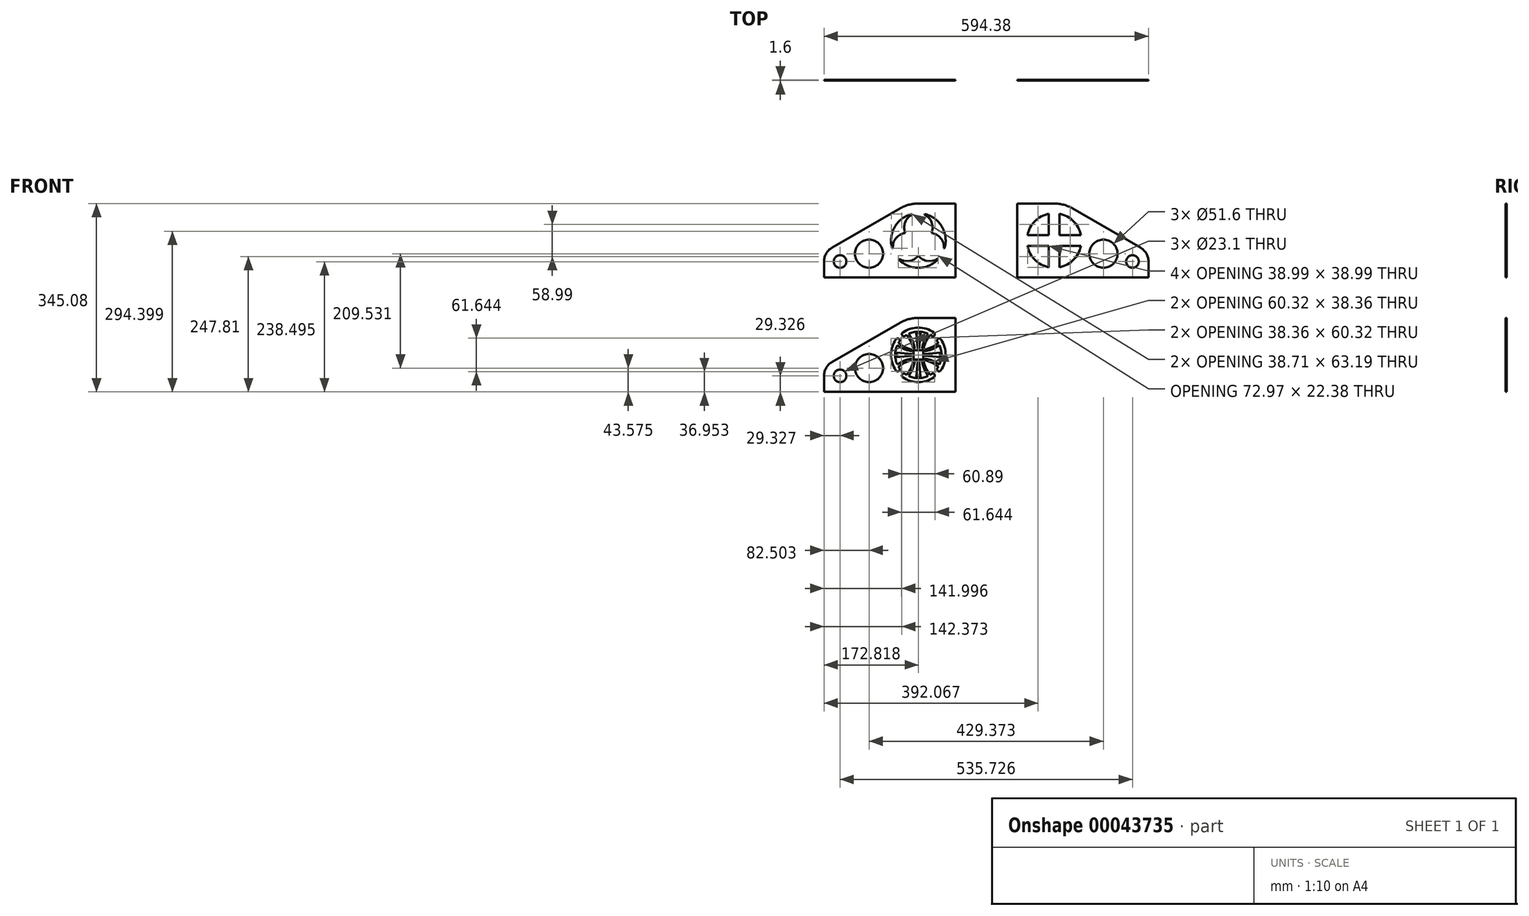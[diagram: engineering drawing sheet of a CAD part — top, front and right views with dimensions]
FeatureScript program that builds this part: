
annotation { "Feature Type Name" : "Feature", "Feature Type Description" : "" }
export const myFeature = defineFeature(function(context is Context, id is Id, definition is map)
    precondition{}
    {
        {
            var Q0;
            Q0=qCreatedBy(makeId("Front.planeOp"),FACE);
            var sketch = newSketch(context, id + "F0", { "sketchPlane" : qUnion([Q0])});
            skLineSegment(sketch, "E0", {"start": v(-56.6, -172.54) * mm, "end": v(-297.19, -172.54) * mm});
            skLineSegment(sketch, "E1", {"start": v(-124.37, -37) * mm, "end": v(-56.6, -37) * mm});
            skArc(sketch, "E2", {"start": v(-124.37, -37) * mm, "mid": v(-141.91, -39.3) * mm, "end": v(-158.26, -46.07) * mm});
            skLineSegment(sketch, "E3", {"start": v(-282.52, -117.82) * mm, "end": v(-158.26, -46.07) * mm});
            skArc(sketch, "E4", {"start": v(-282.52, -117.82) * mm, "mid": v(-293.26, -128.55) * mm, "end": v(-297.19, -143.21) * mm});
            skLineSegment(sketch, "E5", {"start": v(-297.19, -143.21) * mm, "end": v(-297.19, -172.54) * mm});
            skCircle(sketch, "E6", {"center": v(-214.69, -128.97) * mm, "radius": 25.8 * mm});
            skCircle(sketch, "E7", {"center": v(-267.86, -143.21) * mm, "radius": 11.55 * mm});
            skLineSegment(sketch, "E8", {"start": v(-56.6, -37) * mm, "end": v(-56.6, -172.54) * mm});
            skLineSegment(sketch, "E9", {"start": v(-56.6, 37) * mm, "end": v(-297.19, 37) * mm});
            skArc(sketch, "E10", {"start": v(-135.74, 153.46) * mm, "mid": v(-167.67, 129.77) * mm, "end": v(-172.22, 90.26) * mm});
            skArc(sketch, "E11", {"start": v(-100.45, 118.58) * mm, "mid": v(-100.07, 138.01) * mm, "end": v(-113.28, 152.28) * mm});
            skArc(sketch, "E12", {"start": v(-124.37, 77.14) * mm, "mid": v(-107.73, 67.1) * mm, "end": v(-88.77, 71.4) * mm});
            skArc(sketch, "E13", {"start": v(-148.3, 118.58) * mm, "mid": v(-165.32, 109.18) * mm, "end": v(-171.07, 90.61) * mm});
            skLineSegment(sketch, "E14", {"start": v(-135.46, 152.28) * mm, "end": v(-135.74, 153.46) * mm});
            skLineSegment(sketch, "E15", {"start": v(-113.28, 152.28) * mm, "end": v(-113, 153.46) * mm});
            skArc(sketch, "E16", {"start": v(-135.46, 152.28) * mm, "mid": v(-148.67, 138.01) * mm, "end": v(-148.3, 118.58) * mm});
            skLineSegment(sketch, "E17", {"start": v(-159.98, 71.4) * mm, "end": v(-160.86, 70.58) * mm});
            skLineSegment(sketch, "E18", {"start": v(-171.07, 90.61) * mm, "end": v(-172.22, 90.26) * mm});
            skLineSegment(sketch, "E19", {"start": v(-77.68, 90.61) * mm, "end": v(-76.52, 90.26) * mm});
            skLineSegment(sketch, "E20", {"start": v(-88.77, 71.4) * mm, "end": v(-87.89, 70.58) * mm});
            skArc(sketch, "E21", {"start": v(-76.52, 90.26) * mm, "mid": v(-81.07, 129.77) * mm, "end": v(-113, 153.46) * mm});
            skArc(sketch, "E22", {"start": v(-77.68, 90.61) * mm, "mid": v(-83.43, 109.18) * mm, "end": v(-100.45, 118.58) * mm});
            skArc(sketch, "E23", {"start": v(-159.98, 71.4) * mm, "mid": v(-141.02, 67.1) * mm, "end": v(-124.37, 77.14) * mm});
            skArc(sketch, "E24", {"start": v(-160.86, 70.58) * mm, "mid": v(-124.37, 54.77) * mm, "end": v(-87.89, 70.58) * mm});
            skLineSegment(sketch, "E25", {"start": v(-124.37, 172.54) * mm, "end": v(-56.6, 172.54) * mm});
            skArc(sketch, "E26", {"start": v(-124.37, 172.54) * mm, "mid": v(-141.91, 170.23) * mm, "end": v(-158.26, 163.46) * mm});
            skLineSegment(sketch, "E27", {"start": v(-282.52, 91.71) * mm, "end": v(-158.26, 163.46) * mm});
            skArc(sketch, "E28", {"start": v(-282.52, 91.71) * mm, "mid": v(-293.26, 80.98) * mm, "end": v(-297.19, 66.32) * mm});
            skLineSegment(sketch, "E29", {"start": v(-297.19, 66.32) * mm, "end": v(-297.19, 37) * mm});
            skCircle(sketch, "E30", {"center": v(-214.69, 80.57) * mm, "radius": 25.8 * mm});
            skCircle(sketch, "E31", {"center": v(-267.86, 66.32) * mm, "radius": 11.55 * mm});
            skLineSegment(sketch, "E32", {"start": v(-56.6, 172.54) * mm, "end": v(-56.6, 37) * mm});
            skLineSegment(sketch, "E33", {"start": v(282.52, 91.71) * mm, "end": v(158.26, 163.46) * mm});
            skLineSegment(sketch, "E34", {"start": v(297.19, 37) * mm, "end": v(56.6, 37) * mm});
            skArc(sketch, "E35", {"start": v(134.37, 55.78) * mm, "mid": v(159.73, 69.41) * mm, "end": v(173.36, 94.77) * mm});
            skLineSegment(sketch, "E36", {"start": v(75.38, 114.77) * mm, "end": v(114.37, 114.77) * mm});
            skLineSegment(sketch, "E37", {"start": v(75.38, 94.77) * mm, "end": v(114.37, 94.77) * mm});
            skLineSegment(sketch, "E38", {"start": v(134.37, 153.76) * mm, "end": v(134.37, 114.77) * mm});
            skLineSegment(sketch, "E39", {"start": v(114.37, 153.76) * mm, "end": v(114.37, 114.77) * mm});
            skLineSegment(sketch, "E40", {"start": v(134.37, 94.77) * mm, "end": v(173.36, 94.77) * mm});
            skLineSegment(sketch, "E41", {"start": v(114.37, 94.77) * mm, "end": v(114.37, 55.78) * mm});
            skLineSegment(sketch, "E42", {"start": v(134.37, 114.77) * mm, "end": v(173.36, 114.77) * mm});
            skLineSegment(sketch, "E43", {"start": v(134.37, 94.77) * mm, "end": v(134.37, 55.78) * mm});
            skArc(sketch, "E44", {"start": v(75.38, 94.77) * mm, "mid": v(89.02, 69.41) * mm, "end": v(114.37, 55.78) * mm});
            skArc(sketch, "E45", {"start": v(114.37, 153.76) * mm, "mid": v(89.02, 140.12) * mm, "end": v(75.38, 114.77) * mm});
            skArc(sketch, "E46", {"start": v(173.36, 114.77) * mm, "mid": v(159.73, 140.12) * mm, "end": v(134.37, 153.76) * mm});
            skCircle(sketch, "E47", {"center": v(214.69, 80.57) * mm, "radius": 25.8 * mm});
            skCircle(sketch, "E48", {"center": v(267.86, 66.32) * mm, "radius": 11.55 * mm});
            skArc(sketch, "E49", {"start": v(158.26, 163.46) * mm, "mid": v(141.91, 170.23) * mm, "end": v(124.37, 172.54) * mm});
            skLineSegment(sketch, "E50", {"start": v(124.37, 172.54) * mm, "end": v(56.6, 172.54) * mm});
            skArc(sketch, "E51", {"start": v(297.19, 66.32) * mm, "mid": v(293.26, 80.98) * mm, "end": v(282.52, 91.71) * mm});
            skLineSegment(sketch, "E52", {"start": v(297.19, 66.32) * mm, "end": v(297.19, 37) * mm});
            skLineSegment(sketch, "E53", {"start": v(56.6, 172.54) * mm, "end": v(56.6, 37) * mm});
            skArc(sketch, "E54", {"start": v(-134.02, -93.12) * mm, "mid": v(-138.57, -79.96) * mm, "end": v(-146.3, -68.38) * mm});
            skArc(sketch, "E55", {"start": v(-131.07, -93.12) * mm, "mid": v(-135.05, -79.02) * mm, "end": v(-142, -66.12) * mm});
            skLineSegment(sketch, "E56", {"start": v(-128.36, -64.84) * mm, "end": v(-125.85, -93.12) * mm});
            skArc(sketch, "E57", {"start": v(-102.45, -68.38) * mm, "mid": v(-110.18, -79.96) * mm, "end": v(-114.73, -93.12) * mm});
            skArc(sketch, "E58", {"start": v(-106.74, -66.12) * mm, "mid": v(-113.7, -79.02) * mm, "end": v(-117.67, -93.12) * mm});
            skLineSegment(sketch, "E59", {"start": v(-120.39, -64.84) * mm, "end": v(-122.9, -93.12) * mm});
            skLineSegment(sketch, "E60", {"start": v(-128.36, -64.84) * mm, "end": v(-120.39, -64.84) * mm});
            skLineSegment(sketch, "E61", {"start": v(-133.07, -96.07) * mm, "end": v(-133.07, -113.46) * mm});
            skLineSegment(sketch, "E62", {"start": v(-133.07, -113.46) * mm, "end": v(-115.68, -113.46) * mm});
            skLineSegment(sketch, "E63", {"start": v(-115.68, -113.46) * mm, "end": v(-115.68, -96.07) * mm});
            skLineSegment(sketch, "E64", {"start": v(-115.68, -96.07) * mm, "end": v(-133.07, -96.07) * mm});
            skArc(sketch, "E65", {"start": v(-100.06, -69.93) * mm, "mid": v(-94.83, -69) * mm, "end": v(-95.76, -63.76) * mm});
            skArc(sketch, "E66", {"start": v(-152.98, -63.76) * mm, "mid": v(-153.92, -69) * mm, "end": v(-148.68, -69.93) * mm});
            skArc(sketch, "E67", {"start": v(-95.76, -63.76) * mm, "mid": v(-124.37, -54.77) * mm, "end": v(-152.98, -63.76) * mm});
            skArc(sketch, "E68", {"start": v(-100.06, -69.93) * mm, "mid": v(-101.25, -69.13) * mm, "end": v(-102.45, -68.38) * mm});
            skArc(sketch, "E69", {"start": v(-146.3, -68.38) * mm, "mid": v(-147.5, -69.13) * mm, "end": v(-148.68, -69.93) * mm});
            skArc(sketch, "E70", {"start": v(-136.02, -114.4) * mm, "mid": v(-149.17, -118.96) * mm, "end": v(-160.76, -126.68) * mm});
            skArc(sketch, "E71", {"start": v(-106.74, -66.12) * mm, "mid": v(-124.37, -62.29) * mm, "end": v(-142, -66.12) * mm});
            skArc(sketch, "E72", {"start": v(-136.02, -111.46) * mm, "mid": v(-150.12, -115.44) * mm, "end": v(-163.02, -122.4) * mm});
            skLineSegment(sketch, "E73", {"start": v(-164.3, -108.75) * mm, "end": v(-136.02, -106.24) * mm});
            skArc(sketch, "E74", {"start": v(-160.76, -82.85) * mm, "mid": v(-149.17, -90.57) * mm, "end": v(-136.02, -95.12) * mm});
            skArc(sketch, "E75", {"start": v(-163.02, -87.13) * mm, "mid": v(-150.12, -94.09) * mm, "end": v(-136.02, -98.07) * mm});
            skLineSegment(sketch, "E76", {"start": v(-164.3, -100.78) * mm, "end": v(-136.02, -103.3) * mm});
            skLineSegment(sketch, "E77", {"start": v(-164.3, -108.75) * mm, "end": v(-164.3, -100.78) * mm});
            skArc(sketch, "E78", {"start": v(-165.38, -133.38) * mm, "mid": v(-160.14, -134.3) * mm, "end": v(-159.2, -129.07) * mm});
            skArc(sketch, "E79", {"start": v(-159.2, -80.46) * mm, "mid": v(-160.14, -75.22) * mm, "end": v(-165.38, -76.15) * mm});
            skArc(sketch, "E80", {"start": v(-165.38, -76.15) * mm, "mid": v(-174.37, -104.77) * mm, "end": v(-165.38, -133.38) * mm});
            skArc(sketch, "E81", {"start": v(-159.2, -80.46) * mm, "mid": v(-160, -81.64) * mm, "end": v(-160.76, -82.85) * mm});
            skArc(sketch, "E82", {"start": v(-160.76, -126.68) * mm, "mid": v(-160, -127.9) * mm, "end": v(-159.2, -129.07) * mm});
            skArc(sketch, "E83", {"start": v(-163.02, -87.13) * mm, "mid": v(-166.85, -104.77) * mm, "end": v(-163.02, -122.4) * mm});
            skArc(sketch, "E84", {"start": v(-114.73, -116.4) * mm, "mid": v(-110.18, -129.57) * mm, "end": v(-102.45, -141.15) * mm});
            skArc(sketch, "E85", {"start": v(-117.67, -116.4) * mm, "mid": v(-113.7, -130.51) * mm, "end": v(-106.74, -143.41) * mm});
            skLineSegment(sketch, "E86", {"start": v(-120.39, -144.7) * mm, "end": v(-122.9, -116.4) * mm});
            skArc(sketch, "E87", {"start": v(-146.3, -141.15) * mm, "mid": v(-138.57, -129.57) * mm, "end": v(-134.02, -116.4) * mm});
            skArc(sketch, "E88", {"start": v(-142, -143.41) * mm, "mid": v(-135.05, -130.51) * mm, "end": v(-131.07, -116.4) * mm});
            skLineSegment(sketch, "E89", {"start": v(-128.36, -144.7) * mm, "end": v(-125.85, -116.4) * mm});
            skLineSegment(sketch, "E90", {"start": v(-120.39, -144.7) * mm, "end": v(-128.36, -144.7) * mm});
            skArc(sketch, "E91", {"start": v(-95.76, -145.77) * mm, "mid": v(-94.83, -140.53) * mm, "end": v(-100.06, -139.6) * mm});
            skArc(sketch, "E92", {"start": v(-148.68, -139.6) * mm, "mid": v(-153.92, -140.53) * mm, "end": v(-152.98, -145.77) * mm});
            skArc(sketch, "E93", {"start": v(-152.98, -145.77) * mm, "mid": v(-124.37, -154.77) * mm, "end": v(-95.76, -145.77) * mm});
            skArc(sketch, "E94", {"start": v(-148.68, -139.6) * mm, "mid": v(-147.5, -140.4) * mm, "end": v(-146.3, -141.15) * mm});
            skArc(sketch, "E95", {"start": v(-102.45, -141.15) * mm, "mid": v(-101.25, -140.4) * mm, "end": v(-100.06, -139.6) * mm});
            skArc(sketch, "E96", {"start": v(-142, -143.41) * mm, "mid": v(-124.37, -147.24) * mm, "end": v(-106.74, -143.41) * mm});
            skArc(sketch, "E97", {"start": v(-112.73, -95.12) * mm, "mid": v(-99.57, -90.57) * mm, "end": v(-87.99, -82.85) * mm});
            skArc(sketch, "E98", {"start": v(-112.73, -98.07) * mm, "mid": v(-98.62, -94.09) * mm, "end": v(-85.73, -87.13) * mm});
            skLineSegment(sketch, "E99", {"start": v(-84.44, -100.78) * mm, "end": v(-112.73, -103.3) * mm});
            skArc(sketch, "E100", {"start": v(-87.99, -126.68) * mm, "mid": v(-99.57, -118.96) * mm, "end": v(-112.73, -114.4) * mm});
            skArc(sketch, "E101", {"start": v(-85.73, -122.4) * mm, "mid": v(-98.62, -115.44) * mm, "end": v(-112.73, -111.46) * mm});
            skLineSegment(sketch, "E102", {"start": v(-84.44, -108.75) * mm, "end": v(-112.73, -106.24) * mm});
            skLineSegment(sketch, "E103", {"start": v(-84.44, -100.78) * mm, "end": v(-84.44, -108.75) * mm});
            skArc(sketch, "E104", {"start": v(-83.37, -76.15) * mm, "mid": v(-88.6, -75.22) * mm, "end": v(-89.54, -80.46) * mm});
            skArc(sketch, "E105", {"start": v(-89.54, -129.07) * mm, "mid": v(-88.6, -134.3) * mm, "end": v(-83.37, -133.38) * mm});
            skArc(sketch, "E106", {"start": v(-83.37, -133.38) * mm, "mid": v(-74.37, -104.77) * mm, "end": v(-83.37, -76.15) * mm});
            skArc(sketch, "E107", {"start": v(-89.54, -129.07) * mm, "mid": v(-88.74, -127.9) * mm, "end": v(-87.99, -126.68) * mm});
            skArc(sketch, "E108", {"start": v(-87.99, -82.85) * mm, "mid": v(-88.74, -81.64) * mm, "end": v(-89.54, -80.46) * mm});
            skArc(sketch, "E109", {"start": v(-85.73, -122.4) * mm, "mid": v(-81.9, -104.77) * mm, "end": v(-85.73, -87.13) * mm});
            skLineSegment(sketch, "E110", {"start": v(-114.73, -116.4) * mm, "end": v(-117.67, -116.4) * mm});
            skLineSegment(sketch, "E111", {"start": v(-112.73, -111.46) * mm, "end": v(-112.73, -114.4) * mm});
            skLineSegment(sketch, "E112", {"start": v(-131.07, -116.4) * mm, "end": v(-134.02, -116.4) * mm});
            skLineSegment(sketch, "E113", {"start": v(-122.9, -116.4) * mm, "end": v(-125.85, -116.4) * mm});
            skLineSegment(sketch, "E114", {"start": v(-112.73, -103.3) * mm, "end": v(-112.73, -106.24) * mm});
            skLineSegment(sketch, "E115", {"start": v(-136.02, -106.24) * mm, "end": v(-136.02, -103.3) * mm});
            skLineSegment(sketch, "E116", {"start": v(-136.02, -114.4) * mm, "end": v(-136.02, -111.46) * mm});
            skLineSegment(sketch, "E117", {"start": v(-112.73, -95.12) * mm, "end": v(-112.73, -98.07) * mm});
            skLineSegment(sketch, "E118", {"start": v(-117.67, -93.12) * mm, "end": v(-114.73, -93.12) * mm});
            skLineSegment(sketch, "E119", {"start": v(-136.02, -95.12) * mm, "end": v(-136.02, -98.07) * mm});
            skLineSegment(sketch, "E120", {"start": v(-125.85, -93.12) * mm, "end": v(-122.9, -93.12) * mm});
            skLineSegment(sketch, "E121", {"start": v(-134.02, -93.12) * mm, "end": v(-131.07, -93.12) * mm});
            skSolve(sketch);
        }
        {
            var Q0;
            Q0=makeQuery(id+"F0.imprint","IMPRINT",FACE,{"disambiguationData":[TD([[makeQuery(id+"F0.imprint","IMPRINT",EDGE,{"derivedFrom":sQuery(id+"F0.wireOp",EDGE,"E9")}),-1.0]])]});
            extrude(context, id + "F1", {"entities" : qUnion([Q0]), "depth" : 1.6 * mm});
        }
        {
            var Q0;
            Q0=makeQuery(id+"F0.imprint","IMPRINT",FACE,{"disambiguationData":[TD([[makeQuery(id+"F0.imprint","IMPRINT",EDGE,{"derivedFrom":sQuery(id+"F0.wireOp",EDGE,"E33")}),1.0]])]});
            extrude(context, id + "F2", {"entities" : qUnion([Q0]), "depth" : 1.6 * mm});
        }
        {
            var Q0;
            Q0=makeQuery(id+"F0.imprint","IMPRINT",FACE,{"disambiguationData":[TD([[makeQuery(id+"F0.imprint","IMPRINT",EDGE,{"derivedFrom":sQuery(id+"F0.wireOp",EDGE,"E0")}),-1.0]])]});
            extrude(context, id + "F3", {"entities" : qUnion([Q0]), "depth" : 1.6 * mm});
        }
        {
            var Q0;
            Q0=makeQuery(id+"F1.opExtrude","SWEPT_FACE",FACE,{"disambiguationData":[OSD([sQuery(id+"F0.wireOp",EDGE,"E25")])]});
            var sketch = newSketch(context, id + "F4", { "sketchPlane" : qUnion([Q0])});
            skLineSegment(sketch, "E122", {"start": v(-56.6, -0.8) * mm, "end": v(-32.45, -0.8) * mm, "construction": true});
            skSolve(sketch);
        }
        {
            var Q0;
            Q0=makeQuery(id+"F2.opExtrude","SWEPT_FACE",FACE,{"disambiguationData":[OSD([sQuery(id+"F0.wireOp",EDGE,"E50")])]});
            var sketch = newSketch(context, id + "F5", { "sketchPlane" : qUnion([Q0])});
            skLineSegment(sketch, "E123", {"start": v(56.6, -0.8) * mm, "end": v(32.45, -0.8) * mm, "construction": true});
            skSolve(sketch);
        }
        {
            var Q0;
            Q0=makeQuery(id+"F3.opExtrude","SWEPT_FACE",FACE,{"disambiguationData":[OSD([sQuery(id+"F0.wireOp",EDGE,"E1")])]});
            var sketch = newSketch(context, id + "F6", { "sketchPlane" : qUnion([Q0])});
            skLineSegment(sketch, "E124", {"start": v(-56.6, -0.8) * mm, "end": v(-32.45, -0.8) * mm, "construction": true});
            skSolve(sketch);
        }
    });
